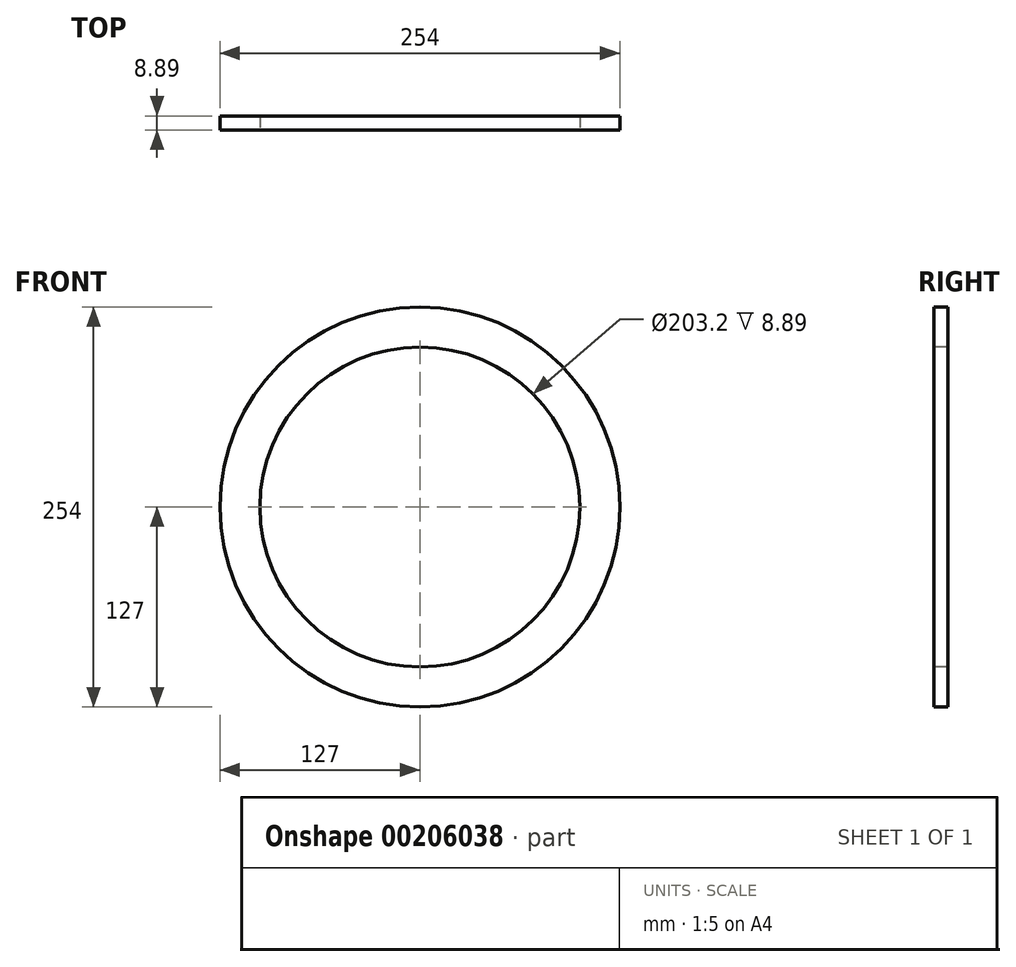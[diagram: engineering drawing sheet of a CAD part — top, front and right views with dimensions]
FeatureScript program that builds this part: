
annotation { "Feature Type Name" : "Feature", "Feature Type Description" : "" }
export const myFeature = defineFeature(function(context is Context, id is Id, definition is map)
    precondition{}
    {
        {
            var Q0;
            Q0=qCreatedBy(makeId("Front.planeOp"),FACE);
            var sketch = newSketch(context, id + "F0", { "sketchPlane" : qUnion([Q0])});
            skCircle(sketch, "E0", {"center": v(0, 0) * mm, "radius": 127 * mm});
            skSolve(sketch);
        }
        {
            var Q0;
            Q0=makeQuery(id+"F0.imprint","IMPRINT",FACE,{"disambiguationData":[TD([[makeQuery(id+"F0.imprint","IMPRINT",EDGE,{"derivedFrom":sQuery(id+"F0.wireOp",EDGE,"E0")}),1.0]])]});
            extrude(context, id + "F1", {"entities" : qUnion([Q0]), "oppositeDirection" : true, "depth" : 34.3 * mm, "hasSecondDirection" : true, "secondDirectionOppositeDirection" : true, "secondDirectionDepth" : 25.4 * mm});
        }
        {
            var Q0;
            Q0=sQuery(id+"F0.wireOp",VERTEX,"E0.center");
            var Q1;
            Q1=makeQuery(id+"F1.opExtrude","SWEPT_BODY",BODY,{"disambiguationData":[OSD([sQuery(id+"F0.wireOp",EDGE,"E0")])]});
            hole(context, id + "F2", {"style" : HoleStyle.SIMPLE, "endStyle" : HoleEndStyle.THROUGH, "holeDiameter" : 203.2 * mm, "locations" : qUnion([Q0]), "scope" : qUnion([Q1]), "isTappedThrough" : true});
        }
    });
